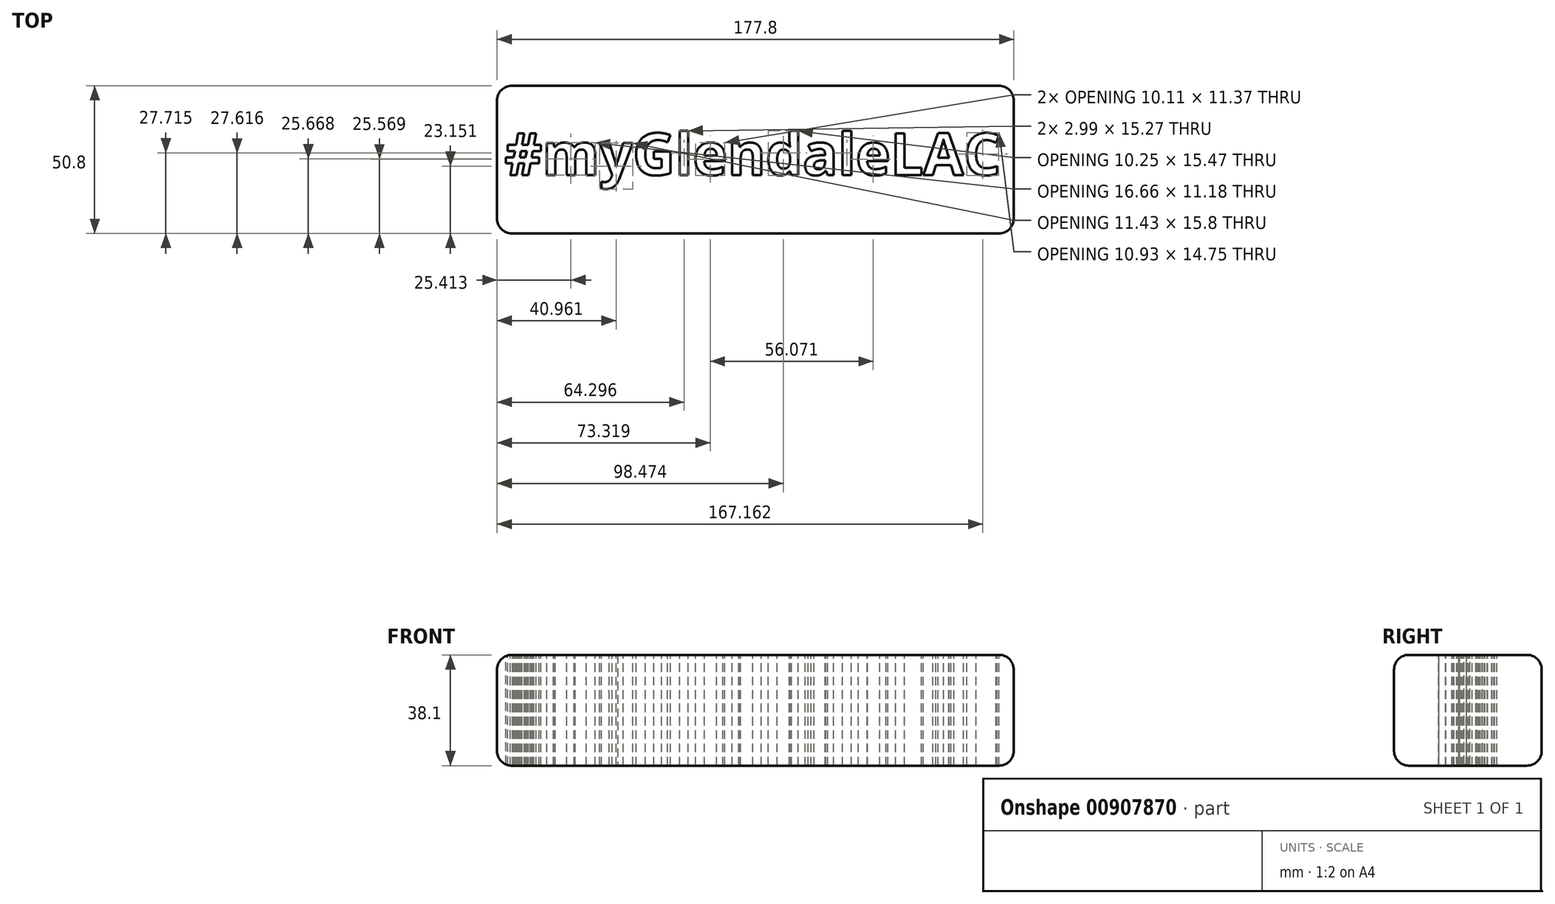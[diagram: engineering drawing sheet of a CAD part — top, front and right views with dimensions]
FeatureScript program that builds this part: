
annotation { "Feature Type Name" : "Feature", "Feature Type Description" : "" }
export const myFeature = defineFeature(function(context is Context, id is Id, definition is map)
    precondition{}
    {
        {
            var Q0;
            Q0=qCreatedBy(makeId("Top.planeOp"),FACE);
            var sketch = newSketch(context, id + "F0", { "sketchPlane" : qUnion([Q0])});
            skLineSegment(sketch, "E0.bottom", {"start": v(88.9, 25.4) * mm, "end": v(-88.9, 25.4) * mm});
            skLineSegment(sketch, "E0.top", {"start": v(88.9, -25.4) * mm, "end": v(-88.9, -25.4) * mm});
            skLineSegment(sketch, "E0.left", {"start": v(88.9, 25.4) * mm, "end": v(88.9, -25.4) * mm});
            skLineSegment(sketch, "E0.right", {"start": v(-88.9, 25.4) * mm, "end": v(-88.9, -25.4) * mm});
            skPoint(sketch, "E0.middle", {"position": v(0, 0) * mm});
            skSolve(sketch);
        }
        {
            var Q0;
            Q0 = qSketchRegion(id + "F0", true);
            extrude(context, id + "F1", {"entities" : qUnion([Q0]), "depth" : 38.1 * mm, "offsetDistance" : 25.4 * mm});
        }
        {
            var Q0;
            Q0=makeQuery(id+"F1.opExtrude","CAP_FACE",FACE,{"disambiguationData":[OSD([sQuery(id+"F0.wireOp",EDGE,"E0.bottom"),sQuery(id+"F0.wireOp",EDGE,"E0.top"),sQuery(id+"F0.wireOp",EDGE,"E0.left"),sQuery(id+"F0.wireOp",EDGE,"E0.right")])],"isStart":false});
            var sketch = newSketch(context, id + "F2", { "sketchPlane" : qUnion([Q0])});
            skText(sketch, "E1", { "text": "#myGlendaleLAC", "fontName": "OpenSans-Bold.ttf"});
            const initialGuessF2  = {"E1": [-0.08637, -0.00532, 1, 0, 0.01447]};
            skSetInitialGuess(sketch, initialGuessF2);
            skSolve(sketch);
        }
        {
            var Q0;
            Q0 = qSketchRegion(id + "F2", true);
            extrude(context, id + "F3", {"entities" : qUnion([Q0]), "operationType" : NewBodyOperationType.REMOVE, "endBound" : BoundingType.UP_TO_NEXT, "oppositeDirection" : true, "depth" : 25.4 * mm, "offsetDistance" : 25.4 * mm});
        }
        {
            var Q0;
            Q0=makeQuery(id+"F1.opExtrude","CAP_EDGE",EDGE,{"disambiguationData":[OSD([sQuery(id+"F0.wireOp",EDGE,"E0.bottom")])],"isStart":false});
            var Q1;
            Q1=makeQuery(id+"F1.opExtrude","CAP_EDGE",EDGE,{"disambiguationData":[OSD([sQuery(id+"F0.wireOp",EDGE,"E0.right")])],"isStart":false});
            var Q2;
            Q2=makeQuery(id+"F1.opExtrude","SWEPT_EDGE",EDGE,{"disambiguationData":[OSD([sQuery(id+"F0.wireOp",EDGE,"E0.bottom"),sQuery(id+"F0.wireOp",EDGE,"E0.right")])]});
            var Q3;
            Q3=makeQuery(id+"F1.opExtrude","CAP_EDGE",EDGE,{"disambiguationData":[OSD([sQuery(id+"F0.wireOp",EDGE,"E0.right")])],"isStart":true});
            var Q4;
            Q4=makeQuery(id+"F1.opExtrude","SWEPT_FACE",FACE,{"disambiguationData":[OSD([sQuery(id+"F0.wireOp",EDGE,"E0.top")])]});
            var Q5;
            Q5=makeQuery(id+"F1.opExtrude","SWEPT_FACE",FACE,{"disambiguationData":[OSD([sQuery(id+"F0.wireOp",EDGE,"E0.left")])]});
            var Q6;
            Q6=makeQuery(id+"F1.opExtrude","CAP_EDGE",EDGE,{"disambiguationData":[OSD([sQuery(id+"F0.wireOp",EDGE,"E0.bottom")])],"isStart":true});
            fillet(context, id + "F4", {"entities" : qUnion([Q0, Q1, Q2, Q3, Q4, Q5, Q6]), "radius" : 5.08 * mm, "tangentPropagation" : true, "allowEdgeOverflow" : false});
        }
    });
